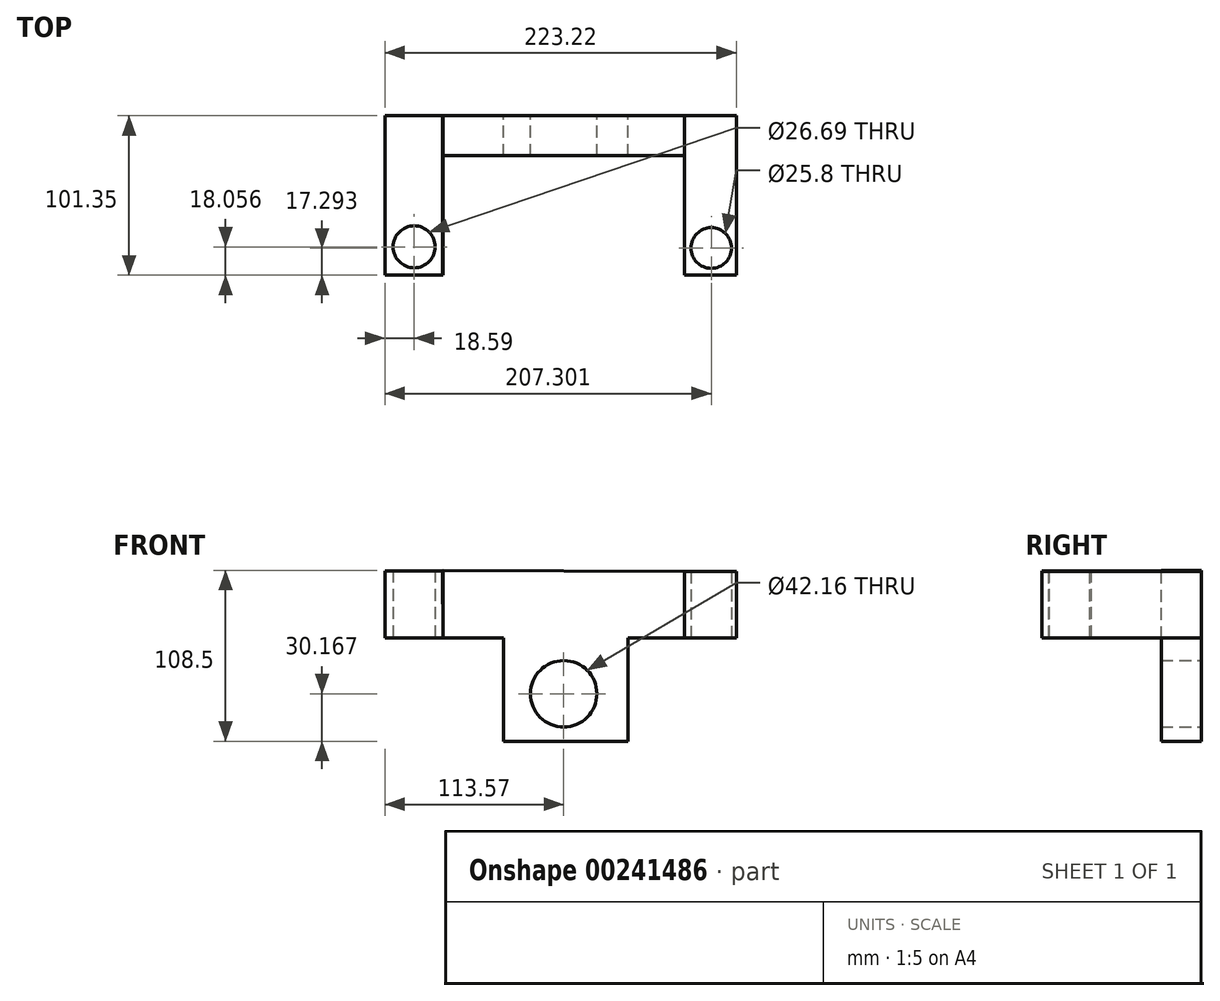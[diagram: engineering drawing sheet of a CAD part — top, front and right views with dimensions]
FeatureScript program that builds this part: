
annotation { "Feature Type Name" : "Feature", "Feature Type Description" : "" }
export const myFeature = defineFeature(function(context is Context, id is Id, definition is map)
    precondition{}
    {
        {
            var Q0;
            Q0=qCreatedBy(makeId("Front.planeOp"),FACE);
            var sketch = newSketch(context, id + "F0", { "sketchPlane" : qUnion([Q0])});
            skLineSegment(sketch, "E0", {"start": v(-38.35, -65.57) * mm, "end": v(40.7, -65.57) * mm});
            skLineSegment(sketch, "E1", {"start": v(-38.35, -65.57) * mm, "end": v(-38.35, 0) * mm});
            skLineSegment(sketch, "E2", {"start": v(40.7, -65.57) * mm, "end": v(40.7, 0) * mm});
            skLineSegment(sketch, "E3", {"start": v(-38.35, 0) * mm, "end": v(-76.53, 0) * mm});
            skLineSegment(sketch, "E4", {"start": v(40.7, 0) * mm, "end": v(76.8, 0) * mm});
            skLineSegment(sketch, "E5", {"start": v(-76.53, 0) * mm, "end": v(-76.53, 42.93) * mm});
            skLineSegment(sketch, "E6", {"start": v(76.8, 0) * mm, "end": v(76.8, 42.28) * mm});
            skLineSegment(sketch, "E7", {"start": v(-76.53, 42.93) * mm, "end": v(76.8, 42.28) * mm});
            skSolve(sketch);
        }
        {
            var Q0;
            Q0 = qSketchRegion(id + "F0", true);
            extrude(context, id + "F1", {"entities" : qUnion([Q0]), "depth" : 25.4 * mm});
        }
        {
            var Q0;
            Q0=qCreatedBy(makeId("Front.planeOp"),FACE);
            var sketch = newSketch(context, id + "F2", { "sketchPlane" : qUnion([Q0])});
            skLineSegment(sketch, "E8", {"start": v(76.53, 42.3) * mm, "end": v(109.65, 42.3) * mm});
            skLineSegment(sketch, "E9", {"start": v(76.53, 0) * mm, "end": v(109.65, 0) * mm});
            skLineSegment(sketch, "E10", {"start": v(109.65, 42.3) * mm, "end": v(109.65, 0) * mm});
            skLineSegment(sketch, "E11", {"start": v(76.53, 42.3) * mm, "end": v(76.53, 0) * mm});
            skLineSegment(sketch, "E12", {"start": v(-76.84, 42.64) * mm, "end": v(-113.57, 42.64) * mm});
            skLineSegment(sketch, "E13", {"start": v(-113.57, 42.64) * mm, "end": v(-113.57, 0) * mm});
            skLineSegment(sketch, "E14", {"start": v(-113.57, 0) * mm, "end": v(-76.67, 0) * mm});
            skLineSegment(sketch, "E15", {"start": v(-76.67, 0) * mm, "end": v(-76.84, 42.64) * mm});
            skSolve(sketch);
        }
        {
            var Q0;
            Q0 = qSketchRegion(id + "F2", true);
            extrude(context, id + "F3", {"entities" : qUnion([Q0]), "operationType" : NewBodyOperationType.ADD, "depth" : 101.35 * mm});
        }
        {
            var Q0;
            Q0=qCreatedBy(makeId("Top.planeOp"),FACE);
            var sketch = newSketch(context, id + "F4", { "sketchPlane" : qUnion([Q0])});
            skCircle(sketch, "E16", {"center": v(-94.98, -83.3) * mm, "radius": 13.34 * mm});
            skCircle(sketch, "E17", {"center": v(93.73, -84.06) * mm, "radius": 12.9 * mm});
            skSolve(sketch);
        }
        {
            var Q0;
            Q0 = qSketchRegion(id + "F4", true);
            extrude(context, id + "F5", {"entities" : qUnion([Q0]), "operationType" : NewBodyOperationType.REMOVE, "depth" : 128.27 * mm});
        }
        {
            var Q0;
            Q0=qCreatedBy(makeId("Front.planeOp"),FACE);
            var sketch = newSketch(context, id + "F6", { "sketchPlane" : qUnion([Q0])});
            skCircle(sketch, "E18", {"center": v(0, -35.4) * mm, "radius": 21.08 * mm});
            skSolve(sketch);
        }
        {
            var Q0;
            Q0 = qSketchRegion(id + "F6", true);
            extrude(context, id + "F7", {"entities" : qUnion([Q0]), "operationType" : NewBodyOperationType.REMOVE, "depth" : 62.74 * mm});
        }
    });
